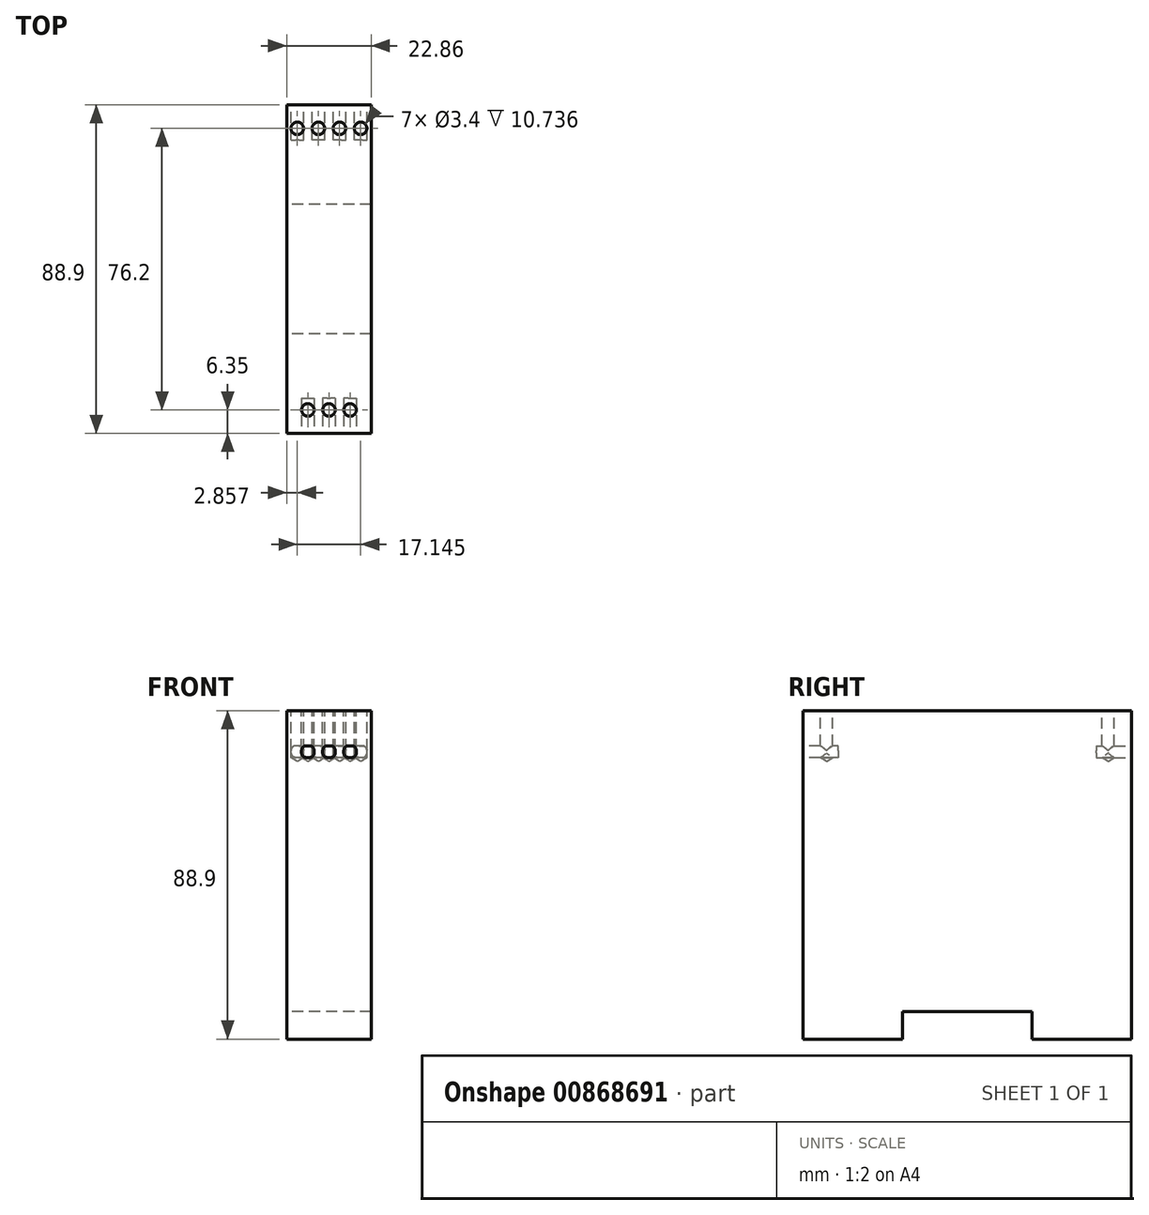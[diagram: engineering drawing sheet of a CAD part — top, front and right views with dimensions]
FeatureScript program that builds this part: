
annotation { "Feature Type Name" : "Feature", "Feature Type Description" : "" }
export const myFeature = defineFeature(function(context is Context, id is Id, definition is map)
    precondition{}
    {
        {
            var Q0;
            Q0=qCreatedBy(makeId("Right.planeOp"),FACE);
            var sketch = newSketch(context, id + "F0", { "sketchPlane" : qUnion([Q0])});
            skLineSegment(sketch, "E0.bottom", {"start": v(-44.45, 44.45) * mm, "end": v(44.45, 44.45) * mm});
            skLineSegment(sketch, "E0.top", {"start": v(-44.45, -44.45) * mm, "end": v(44.45, -44.45) * mm});
            skLineSegment(sketch, "E0.left", {"start": v(-44.45, 44.45) * mm, "end": v(-44.45, -44.45) * mm});
            skLineSegment(sketch, "E0.right", {"start": v(44.45, 44.45) * mm, "end": v(44.45, -44.45) * mm});
            skPoint(sketch, "E0.middle", {"position": v(0, 0) * mm});
            skLineSegment(sketch, "E1.bottom", {"start": v(-17.5, -44.45) * mm, "end": v(17.5, -44.45) * mm});
            skLineSegment(sketch, "E1.top", {"start": v(-17.5, -36.95) * mm, "end": v(17.5, -36.95) * mm});
            skLineSegment(sketch, "E1.left", {"start": v(-17.5, -44.45) * mm, "end": v(-17.5, -36.95) * mm});
            skLineSegment(sketch, "E1.right", {"start": v(17.5, -44.45) * mm, "end": v(17.5, -36.95) * mm});
            skSolve(sketch);
        }
        {
            var Q0;
            Q0=makeQuery(id+"F0.imprint","IMPRINT",FACE,{"disambiguationData":[TD([[makeQuery(id+"F0.imprint","IMPRINT",EDGE,{"derivedFrom":sQuery(id+"F0.wireOp",EDGE,"E0.bottom")}),-1.0]])]});
            extrude(context, id + "F1", {"entities" : qUnion([Q0]), "depth" : 22.86 * mm, "offsetDistance" : 25.4 * mm});
        }
        {
            var Q0;
            Q0=makeQuery(id+"F1.opExtrude","SWEPT_FACE",FACE,{"disambiguationData":[OSD([sQuery(id+"F0.wireOp",EDGE,"E0.bottom")])]});
            var sketch = newSketch(context, id + "F2", { "sketchPlane" : qUnion([Q0])});
            skPoint(sketch, "E2", {"position": v(11.43, -38.1) * mm});
            skPoint(sketch, "E2.positionSnap0", {"position": v(11.43, -44.45) * mm});
            skPoint(sketch, "E3", {"position": v(5.72, -38.1) * mm});
            skPoint(sketch, "E4", {"position": v(17.14, -38.1) * mm});
            skPoint(sketch, "E5", {"position": v(2.86, 38.1) * mm});
            skPoint(sketch, "E6", {"position": v(8.57, 38.1) * mm});
            skPoint(sketch, "E7", {"position": v(14.29, 38.1) * mm});
            skPoint(sketch, "E8", {"position": v(20, 38.1) * mm});
            skSolve(sketch);
        }
        {
            var Q0;
            Q0=sQuery(id+"F2.wireOp",VERTEX,"E5");
            var Q1;
            Q1=sQuery(id+"F2.wireOp",VERTEX,"E6");
            var Q2;
            Q2=sQuery(id+"F2.wireOp",VERTEX,"E7");
            var Q3;
            Q3=sQuery(id+"F2.wireOp",VERTEX,"E8");
            var Q4;
            Q4=sQuery(id+"F2.wireOp",VERTEX,"E3");
            var Q5;
            Q5=sQuery(id+"F2.wireOp",VERTEX,"E2");
            var Q6;
            Q6=sQuery(id+"F2.wireOp",VERTEX,"E4");
            var Q7;
            Q7=makeQuery(id+"F1.opExtrude","SWEPT_BODY",BODY,{"disambiguationData":[OSD([sQuery(id+"F0.wireOp",EDGE,"E0.bottom"),sQuery(id+"F0.wireOp",EDGE,"E0.top"),sQuery(id+"F0.wireOp",EDGE,"E0.left"),sQuery(id+"F0.wireOp",EDGE,"E0.right"),sQuery(id+"F0.wireOp",EDGE,"E1.top"),sQuery(id+"F0.wireOp",EDGE,"E1.left"),sQuery(id+"F0.wireOp",EDGE,"E1.right")])]});
            hole(context, id + "F3", {"style" : HoleStyle.SIMPLE, "endStyle" : HoleEndStyle.BLIND, "standardTappedOrClearance" : lookupTablePath({ "fit" : "Normal", "standard" : "ISO", "size" : "M3", "type" : "Clearance" }), "standardBlindInLast" : lookupTablePath({ "fit" : "Normal", "standard" : "ISO", "size" : "M3", "type" : "Clearance" }), "holeDiameter" : 3.4 * mm, "majorDiameter" : 6.35 * mm, "holeDepth" : 12.7 * mm, "isTappedThrough" : true, "tappedDepth" : 12.7 * mm, "tapClearance" : 3, "locations" : qUnion([Q0, Q1, Q2, Q3, Q4, Q5, Q6]), "scope" : qUnion([Q7])});
        }
        {
            var Q0;
            Q0=makeQuery(id+"F1.opExtrude","SWEPT_FACE",FACE,{"disambiguationData":[OSD([sQuery(id+"F0.wireOp",EDGE,"E0.left")])]});
            var sketch = newSketch(context, id + "F4", { "sketchPlane" : qUnion([Q0])});
            skLineSegment(sketch, "E9.bottom", {"start": v(5.28, 34.92) * mm, "end": v(6.15, 34.92) * mm});
            skLineSegment(sketch, "E9.top", {"start": v(4.01, 31.75) * mm, "end": v(7.42, 31.75) * mm});
            skLineSegment(sketch, "E9.left", {"start": v(4.01, 33.65) * mm, "end": v(4.01, 33.02) * mm});
            skLineSegment(sketch, "E9.right", {"start": v(7.42, 33.65) * mm, "end": v(7.42, 33.02) * mm});
            skLineSegment(sketch, "E10.1.0.0", {"start": v(9.73, 33.65) * mm, "end": v(9.73, 33.02) * mm});
            skLineSegment(sketch, "E10.1.0.1", {"start": v(11, 31.75) * mm, "end": v(11.86, 31.75) * mm});
            skLineSegment(sketch, "E10.1.0.2", {"start": v(11, 34.92) * mm, "end": v(11.86, 34.92) * mm});
            skLineSegment(sketch, "E10.1.0.3", {"start": v(13.13, 33.65) * mm, "end": v(13.13, 33.02) * mm});
            skLineSegment(sketch, "E10.2.0.0", {"start": v(15.44, 33.65) * mm, "end": v(15.44, 33.02) * mm});
            skLineSegment(sketch, "E10.2.0.1", {"start": v(16.71, 31.75) * mm, "end": v(17.58, 31.75) * mm});
            skLineSegment(sketch, "E10.2.0.2", {"start": v(16.71, 34.92) * mm, "end": v(17.58, 34.92) * mm});
            skLineSegment(sketch, "E10.2.0.3", {"start": v(18.85, 33.65) * mm, "end": v(18.85, 33.02) * mm});
            skLineSegment(sketch, "E10.direction1", {"start": v(5.28, 31.75) * mm, "end": v(6.15, 31.75) * mm, "construction": true});
            skPoint(sketch, "E11.visualSharp", {"position": v(4.01, 34.92) * mm});
            skArc(sketch, "E11.filletArc", {"start": v(5.28, 34.92) * mm, "mid": v(4.39, 34.55) * mm, "end": v(4.01, 33.65) * mm});
            skPoint(sketch, "E12.visualSharp", {"position": v(7.42, 34.92) * mm});
            skArc(sketch, "E12.filletArc", {"start": v(7.42, 33.65) * mm, "mid": v(7.04, 34.55) * mm, "end": v(6.15, 34.92) * mm});
            skPoint(sketch, "E13.newPointA", {"position": v(9.73, 31.75) * mm});
            skPoint(sketch, "E13.newPointB", {"position": v(7.42, 31.75) * mm});
            skArc(sketch, "E13.filletArc", {"start": v(6.15, 31.75) * mm, "mid": v(7.04, 32.12) * mm, "end": v(7.42, 33.02) * mm});
            skPoint(sketch, "E14.visualSharp", {"position": v(4.01, 31.75) * mm});
            skArc(sketch, "E14.filletArc", {"start": v(4.01, 33.02) * mm, "mid": v(4.39, 32.12) * mm, "end": v(5.28, 31.75) * mm});
            skPoint(sketch, "E15.visualSharp", {"position": v(9.73, 34.92) * mm});
            skArc(sketch, "E15.filletArc", {"start": v(11, 34.92) * mm, "mid": v(10.1, 34.55) * mm, "end": v(9.73, 33.65) * mm});
            skPoint(sketch, "E16.visualSharp", {"position": v(13.13, 34.92) * mm});
            skArc(sketch, "E16.filletArc", {"start": v(13.13, 33.65) * mm, "mid": v(12.76, 34.55) * mm, "end": v(11.86, 34.92) * mm});
            skPoint(sketch, "E17.visualSharp", {"position": v(13.13, 31.75) * mm});
            skArc(sketch, "E17.filletArc", {"start": v(11.86, 31.75) * mm, "mid": v(12.76, 32.12) * mm, "end": v(13.13, 33.02) * mm});
            skArc(sketch, "E18.filletArc", {"start": v(9.73, 33.02) * mm, "mid": v(10.1, 32.12) * mm, "end": v(11, 31.75) * mm});
            skPoint(sketch, "E19.visualSharp", {"position": v(15.44, 31.75) * mm});
            skArc(sketch, "E19.filletArc", {"start": v(15.44, 33.02) * mm, "mid": v(15.82, 32.12) * mm, "end": v(16.71, 31.75) * mm});
            skPoint(sketch, "E20.visualSharp", {"position": v(18.85, 31.75) * mm});
            skArc(sketch, "E20.filletArc", {"start": v(17.58, 31.75) * mm, "mid": v(18.47, 32.12) * mm, "end": v(18.85, 33.02) * mm});
            skPoint(sketch, "E21.visualSharp", {"position": v(18.85, 34.92) * mm});
            skArc(sketch, "E21.filletArc", {"start": v(18.85, 33.65) * mm, "mid": v(18.47, 34.55) * mm, "end": v(17.58, 34.92) * mm});
            skPoint(sketch, "E22.visualSharp", {"position": v(15.44, 34.92) * mm});
            skArc(sketch, "E22.filletArc", {"start": v(16.71, 34.92) * mm, "mid": v(15.82, 34.55) * mm, "end": v(15.44, 33.65) * mm});
            skSolve(sketch);
        }
        {
            var Q0;
            Q0=makeQuery(id+"F4.imprint","IMPRINT",FACE,{"disambiguationData":[TD([[makeQuery(id+"F4.imprint","IMPRINT",EDGE,{"derivedFrom":sQuery(id+"F4.wireOp",EDGE,"E9.bottom")}),-1.0]])]});
            var Q1;
            Q1=makeQuery(id+"F4.imprint","IMPRINT",FACE,{"disambiguationData":[TD([[makeQuery(id+"F4.imprint","IMPRINT",EDGE,{"derivedFrom":sQuery(id+"F4.wireOp",EDGE,"E10.1.0.0")}),1.0]])]});
            var Q2;
            Q2=makeQuery(id+"F4.imprint","IMPRINT",FACE,{"disambiguationData":[TD([[makeQuery(id+"F4.imprint","IMPRINT",EDGE,{"derivedFrom":sQuery(id+"F4.wireOp",EDGE,"E10.2.0.0")}),1.0]])]});
            extrude(context, id + "F5", {"entities" : qUnion([Q0, Q1, Q2]), "operationType" : NewBodyOperationType.REMOVE, "oppositeDirection" : true, "depth" : 9.52 * mm, "offsetDistance" : 25.4 * mm});
        }
        {
            var Q0;
            Q0=makeQuery(id+"F1.opExtrude","SWEPT_FACE",FACE,{"disambiguationData":[OSD([sQuery(id+"F0.wireOp",EDGE,"E0.right")])]});
            var sketch = newSketch(context, id + "F6", { "sketchPlane" : qUnion([Q0])});
            skLineSegment(sketch, "E23.bottom", {"start": v(-21.7, 31.75) * mm, "end": v(-18.3, 31.75) * mm});
            skLineSegment(sketch, "E23.top", {"start": v(-20.43, 34.93) * mm, "end": v(-19.57, 34.93) * mm});
            skLineSegment(sketch, "E23.left", {"start": v(-21.7, 33.02) * mm, "end": v(-21.7, 33.66) * mm});
            skLineSegment(sketch, "E23.right", {"start": v(-18.3, 33.02) * mm, "end": v(-18.3, 33.66) * mm});
            skLineSegment(sketch, "E24.1.0.0", {"start": v(-14.72, 34.93) * mm, "end": v(-13.86, 34.93) * mm});
            skLineSegment(sketch, "E24.1.0.1", {"start": v(-14.72, 31.75) * mm, "end": v(-13.86, 31.75) * mm});
            skLineSegment(sketch, "E24.1.0.2", {"start": v(-12.59, 33.02) * mm, "end": v(-12.59, 33.66) * mm});
            skLineSegment(sketch, "E24.1.0.3", {"start": v(-15.99, 33.02) * mm, "end": v(-15.99, 33.66) * mm});
            skLineSegment(sketch, "E24.2.0.0", {"start": v(-9, 34.93) * mm, "end": v(-8.14, 34.93) * mm});
            skLineSegment(sketch, "E24.2.0.1", {"start": v(-9, 31.75) * mm, "end": v(-8.14, 31.75) * mm});
            skLineSegment(sketch, "E24.2.0.2", {"start": v(-6.87, 33.02) * mm, "end": v(-6.87, 33.66) * mm});
            skLineSegment(sketch, "E24.2.0.3", {"start": v(-10.27, 33.02) * mm, "end": v(-10.27, 33.66) * mm});
            skLineSegment(sketch, "E24.3.0.0", {"start": v(-3.29, 34.93) * mm, "end": v(-2.43, 34.93) * mm});
            skLineSegment(sketch, "E24.3.0.1", {"start": v(-3.29, 31.75) * mm, "end": v(-2.43, 31.75) * mm});
            skLineSegment(sketch, "E24.3.0.2", {"start": v(-1.16, 33.02) * mm, "end": v(-1.16, 33.66) * mm});
            skLineSegment(sketch, "E24.3.0.3", {"start": v(-4.56, 33.02) * mm, "end": v(-4.56, 33.66) * mm});
            skLineSegment(sketch, "E24.direction1", {"start": v(-20.43, 31.75) * mm, "end": v(-19.57, 31.75) * mm, "construction": true});
            skPoint(sketch, "E25.visualSharp", {"position": v(-12.59, 34.93) * mm});
            skArc(sketch, "E25.filletArc", {"start": v(-12.59, 33.66) * mm, "mid": v(-12.96, 34.55) * mm, "end": v(-13.86, 34.93) * mm});
            skPoint(sketch, "E26.visualSharp", {"position": v(-15.99, 34.93) * mm});
            skArc(sketch, "E26.filletArc", {"start": v(-14.72, 34.93) * mm, "mid": v(-15.62, 34.55) * mm, "end": v(-15.99, 33.66) * mm});
            skPoint(sketch, "E27.visualSharp", {"position": v(-15.99, 31.75) * mm});
            skArc(sketch, "E27.filletArc", {"start": v(-15.99, 33.02) * mm, "mid": v(-15.62, 32.12) * mm, "end": v(-14.72, 31.75) * mm});
            skPoint(sketch, "E28.visualSharp", {"position": v(-12.59, 31.75) * mm});
            skArc(sketch, "E28.filletArc", {"start": v(-13.86, 31.75) * mm, "mid": v(-12.96, 32.12) * mm, "end": v(-12.59, 33.02) * mm});
            skPoint(sketch, "E29.visualSharp", {"position": v(-21.7, 31.75) * mm});
            skArc(sketch, "E29.filletArc", {"start": v(-21.7, 33.02) * mm, "mid": v(-21.33, 32.12) * mm, "end": v(-20.43, 31.75) * mm});
            skPoint(sketch, "E30.visualSharp", {"position": v(-21.7, 34.93) * mm});
            skArc(sketch, "E30.filletArc", {"start": v(-20.43, 34.93) * mm, "mid": v(-21.33, 34.55) * mm, "end": v(-21.7, 33.66) * mm});
            skPoint(sketch, "E31.visualSharp", {"position": v(-18.3, 34.93) * mm});
            skArc(sketch, "E31.filletArc", {"start": v(-18.3, 33.66) * mm, "mid": v(-18.67, 34.55) * mm, "end": v(-19.57, 34.92) * mm});
            skPoint(sketch, "E32.newPointA", {"position": v(-18.3, 31.75) * mm});
            skArc(sketch, "E32.filletArc", {"start": v(-19.57, 31.75) * mm, "mid": v(-18.67, 32.12) * mm, "end": v(-18.3, 33.02) * mm});
            skPoint(sketch, "E33.visualSharp", {"position": v(-10.27, 34.93) * mm});
            skArc(sketch, "E33.filletArc", {"start": v(-9, 34.93) * mm, "mid": v(-9.9, 34.55) * mm, "end": v(-10.27, 33.66) * mm});
            skPoint(sketch, "E34.visualSharp", {"position": v(-10.27, 31.75) * mm});
            skArc(sketch, "E34.filletArc", {"start": v(-10.27, 33.02) * mm, "mid": v(-9.9, 32.12) * mm, "end": v(-9, 31.75) * mm});
            skPoint(sketch, "E35.visualSharp", {"position": v(-6.87, 31.75) * mm});
            skArc(sketch, "E35.filletArc", {"start": v(-8.14, 31.75) * mm, "mid": v(-7.24, 32.12) * mm, "end": v(-6.87, 33.02) * mm});
            skPoint(sketch, "E36.visualSharp", {"position": v(-6.87, 34.93) * mm});
            skArc(sketch, "E36.filletArc", {"start": v(-6.87, 33.66) * mm, "mid": v(-7.24, 34.55) * mm, "end": v(-8.14, 34.93) * mm});
            skPoint(sketch, "E37.visualSharp", {"position": v(-4.56, 34.93) * mm});
            skArc(sketch, "E37.filletArc", {"start": v(-3.29, 34.93) * mm, "mid": v(-4.19, 34.55) * mm, "end": v(-4.56, 33.66) * mm});
            skPoint(sketch, "E38.visualSharp", {"position": v(-1.16, 34.93) * mm});
            skArc(sketch, "E38.filletArc", {"start": v(-1.16, 33.66) * mm, "mid": v(-1.53, 34.55) * mm, "end": v(-2.43, 34.93) * mm});
            skPoint(sketch, "E39.visualSharp", {"position": v(-1.16, 31.75) * mm});
            skArc(sketch, "E39.filletArc", {"start": v(-2.43, 31.75) * mm, "mid": v(-1.53, 32.12) * mm, "end": v(-1.16, 33.02) * mm});
            skPoint(sketch, "E40.visualSharp", {"position": v(-4.56, 31.75) * mm});
            skArc(sketch, "E40.filletArc", {"start": v(-4.56, 33.02) * mm, "mid": v(-4.19, 32.12) * mm, "end": v(-3.29, 31.75) * mm});
            skSolve(sketch);
        }
        {
            var Q0;
            Q0=makeQuery(id+"F6.imprint","IMPRINT",FACE,{"disambiguationData":[TD([[makeQuery(id+"F6.imprint","IMPRINT",EDGE,{"derivedFrom":sQuery(id+"F6.wireOp",EDGE,"E23.bottom")}),1.0]])]});
            var Q1;
            Q1=makeQuery(id+"F6.imprint","IMPRINT",FACE,{"disambiguationData":[TD([[makeQuery(id+"F6.imprint","IMPRINT",EDGE,{"derivedFrom":sQuery(id+"F6.wireOp",EDGE,"E24.1.0.0")}),-1.0]])]});
            var Q2;
            Q2=makeQuery(id+"F6.imprint","IMPRINT",FACE,{"disambiguationData":[TD([[makeQuery(id+"F6.imprint","IMPRINT",EDGE,{"derivedFrom":sQuery(id+"F6.wireOp",EDGE,"E24.2.0.0")}),-1.0]])]});
            var Q3;
            Q3=makeQuery(id+"F6.imprint","IMPRINT",FACE,{"disambiguationData":[TD([[makeQuery(id+"F6.imprint","IMPRINT",EDGE,{"derivedFrom":sQuery(id+"F6.wireOp",EDGE,"E24.3.0.0")}),-1.0]])]});
            extrude(context, id + "F7", {"entities" : qUnion([Q0, Q1, Q2, Q3]), "operationType" : NewBodyOperationType.REMOVE, "oppositeDirection" : true, "depth" : 9.52 * mm, "offsetDistance" : 25.4 * mm});
        }
    });
